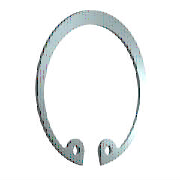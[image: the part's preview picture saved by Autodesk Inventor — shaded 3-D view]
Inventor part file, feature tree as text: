
AUTODESK INVENTOR PART (.ipt)
format: ipt  version: 2024.2 (Build 282272000, 272)  size: 151,552 bytes
history: native  units: mm (DEFAULTED — no unit token found)
features: other x2, plane x1
ambient origin geometry x8: Origin, YZ Plane, XZ Plane, XY Plane, X Axis, Y Axis, Z Axis, Center Point
bodies: Solid1 (feature_tree), Body (feature_tree)
feature tree (3):
  other  "Work Axis1"
  other  "Work Axis2"
  plane  "Work Plane1"
